# Revit family: Shower-Bath_and_Shower_Trim-KOHLER-Alteo-K-TLS45104
name_source: partatom
category: Plumbing Fixtures
revit_build: Autodesk Revit 2017 (Build: 20160225_1515(x64)
units: mm (PartAtom-declared; Revit-internal decimal feet)

## family parameters
Cut with Voids When Loaded = No
Host = Face
OmniClass Number = 23.31.17.00
Part Type = Normal
Room Calculation Point = No
Round Connector Dimension = Use Diameter
Shared = No

## types (3) — shared parameters
ADA Compliant = No
Assembly Code = D2010700
CW Connection = No
Cold Water Inlet = Cold Water Inlet
Date Modified = 07/09/2020
Default Elevation = 42"
Description = Rite-Temp bath and shower valve trim with lever handle and spout, less showerhead
Drain Included = No
Flow Rate = 0 GPM
HW Connection = Yes
Handle Clearance = 3 7/16"
Handle Height = 4 9/16"
Height = 6 7/16"
Hot Water Inlet = Hot Water Inlet
Length = 6 1/2"
Manufacturer = KOHLER Co.
Master Format 2014 = 22 42 23
Master Format 2014 Name = Residential Showers
Material = Premium Metal Construction
Pressure = 0.00 psi
Product Documentation Link = https://www.us.kohler.com
Product Name = Alteo
Product Page URL = http://www.us.kohler.com
Spout Reach = 6 1/2"
Tempered Water Inlet1 = Tempered Water Inlet1
Tempered Water Inlet2 = Tempered Water Inlet2
URL = https://www.us.kohler.com
Vent Connection = No
Waste Connection = No
Waste Water Outlet = Waste Water Outlet
WaterSense Certified = No
Width = 6 7/16"

## per-type parameters (varying)
| type | Finish | Model | Type |
| CP-Polished Chrome | Kohler-Metal-CP-Polished_Chrome | K-TLS45104-4-CP | 1 |
| BN-Vibrant Brushed Nickel | Kohler-Metal-BN-Vibrant_Brushed_Nickel | K-TLS45104-4-BN | 2 |
| 2BZ-Oil Rubbed Bronze | Kohler-Metal-2BZ-Oil_Rubbed_Bronze | K-TLS45104-4-2BZ | 3 |

## geometry (parser evidence)
native form markers: Sweep x7
no freeform markers — native parametric forms only
